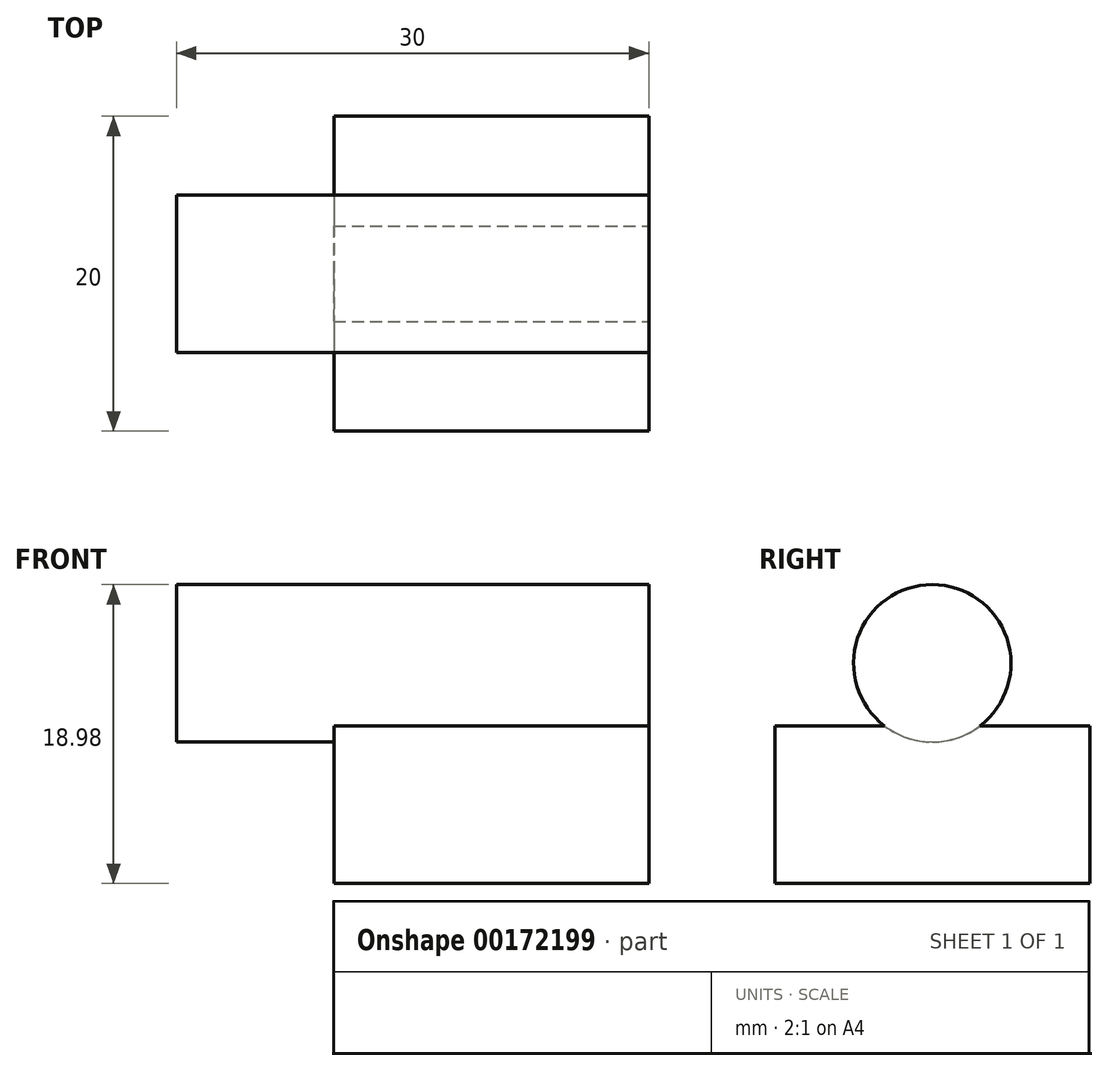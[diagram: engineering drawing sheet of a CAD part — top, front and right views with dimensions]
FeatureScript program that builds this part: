
annotation { "Feature Type Name" : "Feature", "Feature Type Description" : "" }
export const myFeature = defineFeature(function(context is Context, id is Id, definition is map)
    precondition{}
    {
        {
            var Q0;
            Q0=qCreatedBy(makeId("Top.planeOp"),FACE);
            var sketch = newSketch(context, id + "F0", { "sketchPlane" : qUnion([Q0])});
            skLineSegment(sketch, "E0.bottom", {"start": v(10, 10) * mm, "end": v(-10, 10) * mm});
            skLineSegment(sketch, "E0.top", {"start": v(10, -10) * mm, "end": v(-10, -10) * mm});
            skLineSegment(sketch, "E0.left", {"start": v(10, 10) * mm, "end": v(10, -10) * mm});
            skLineSegment(sketch, "E0.right", {"start": v(-10, 10) * mm, "end": v(-10, -10) * mm});
            skPoint(sketch, "E0.middle", {"position": v(0, 0) * mm});
            skSolve(sketch);
        }
        {
            var Q0;
            Q0=qSketchRegion(id+"F0",true);
            extrude(context, id + "F1", {"entities" : qUnion([Q0]), "depth" : 10 * mm});
        }
        {
            var Q0;
            Q0=makeQuery(id+"F1.opExtrude","SWEPT_FACE",FACE,{"disambiguationData":[OSD([sQuery(id+"F0.wireOp",EDGE,"E0.left")])]});
            var sketch = newSketch(context, id + "F2", { "sketchPlane" : qUnion([Q0])});
            skCircle(sketch, "E1", {"center": v(0, 13.98) * mm, "radius": 5 * mm});
            skSolve(sketch);
        }
        {
            var Q0;
            Q0=qSketchRegion(id+"F2",true);
            extrude(context, id + "F3", {"entities" : qUnion([Q0]), "operationType" : NewBodyOperationType.ADD, "oppositeDirection" : true, "depth" : 30 * mm});
        }
    });
